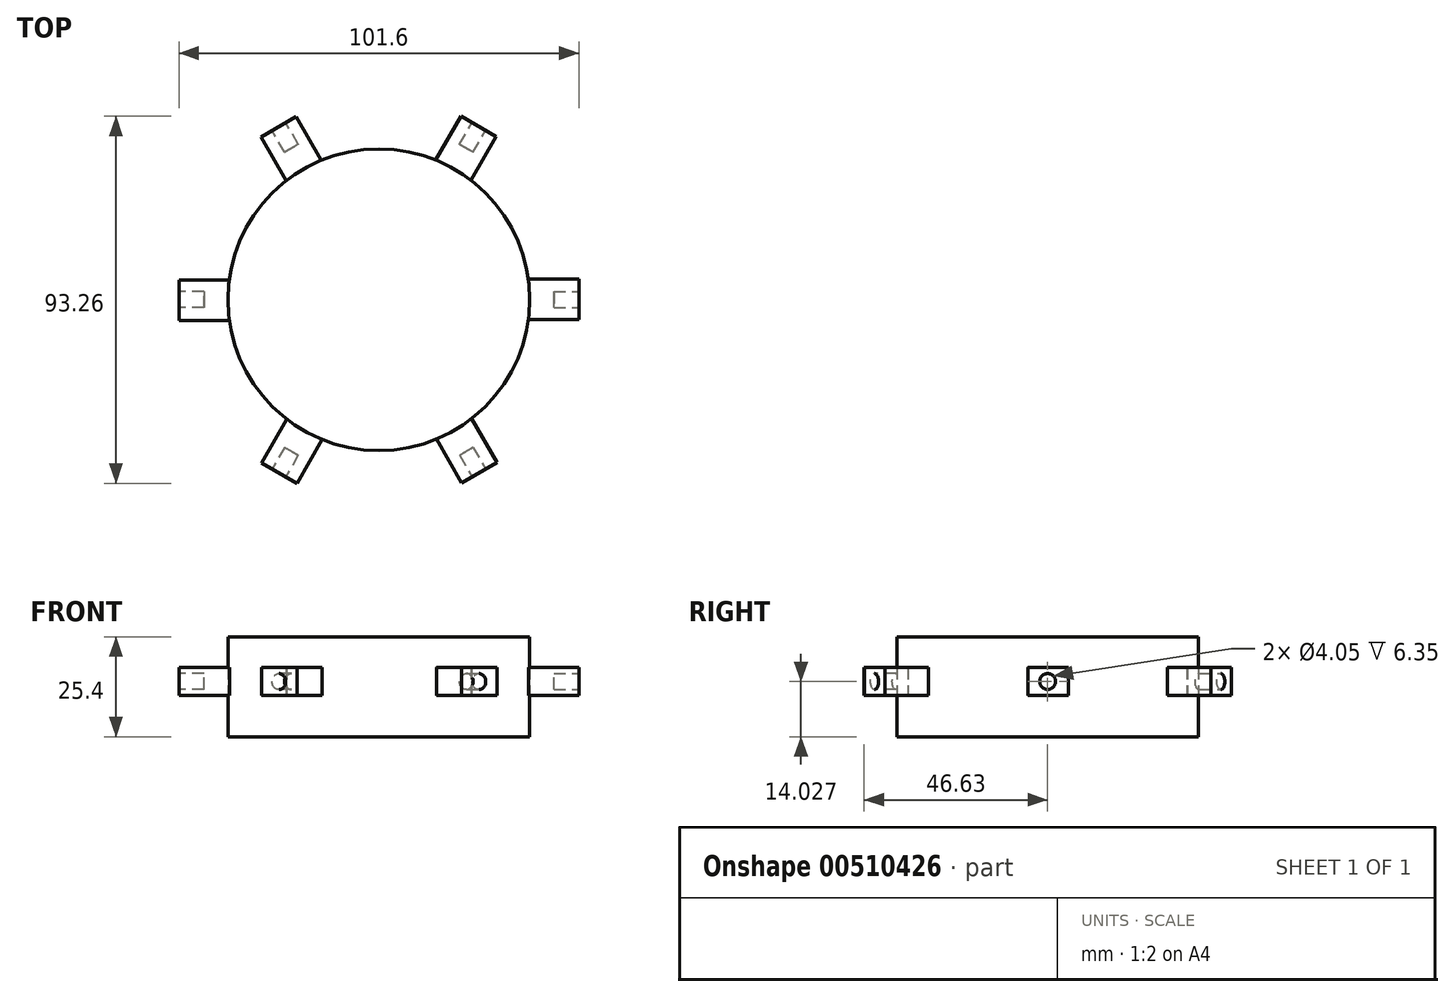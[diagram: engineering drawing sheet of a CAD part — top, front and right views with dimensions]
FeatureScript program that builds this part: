
annotation { "Feature Type Name" : "Feature", "Feature Type Description" : "" }
export const myFeature = defineFeature(function(context is Context, id is Id, definition is map)
    precondition{}
    {
        {
            var Q0;
            Q0=qCreatedBy(makeId("Top.planeOp"),FACE);
            var sketch = newSketch(context, id + "F0", { "sketchPlane" : qUnion([Q0])});
            skCircle(sketch, "E0", {"center": v(0, 0) * mm, "radius": 38.33 * mm});
            skSolve(sketch);
        }
        {
            var Q0;
            Q0=makeQuery(id+"F0.imprint","IMPRINT",FACE,{"disambiguationData":[TD([[makeQuery(id+"F0.imprint","IMPRINT",EDGE,{"derivedFrom":sQuery(id+"F0.wireOp",EDGE,"E0")}),1.0]])]});
            extrude(context, id + "F1", {"entities" : qUnion([Q0]), "depth" : 25.4 * mm});
        }
        {
            var Q0;
            Q0=qCreatedBy(makeId("Right.planeOp"),FACE);
            var sketch = newSketch(context, id + "F2", { "sketchPlane" : qUnion([Q0])});
            skLineSegment(sketch, "E1.bottom", {"start": v(-5.05, 17.62) * mm, "end": v(5.27, 17.62) * mm});
            skLineSegment(sketch, "E1.top", {"start": v(-5.05, 10.44) * mm, "end": v(5.27, 10.44) * mm});
            skLineSegment(sketch, "E1.left", {"start": v(-5.05, 17.62) * mm, "end": v(-5.05, 10.44) * mm});
            skLineSegment(sketch, "E1.right", {"start": v(5.27, 17.62) * mm, "end": v(5.27, 10.44) * mm});
            skSolve(sketch);
        }
        {
            var Q0;
            Q0 = qSketchRegion(id + "F2", true);
            extrude(context, id + "F3", {"entities" : qUnion([Q0]), "operationType" : NewBodyOperationType.ADD, "depth" : 50.8 * mm});
        }
        {
            var Q0;
            Q0=makeQuery(id+"F3.opExtrude","CAP_FACE",FACE,{"disambiguationData":[OSD([sQuery(id+"F2.wireOp",EDGE,"E1.bottom"),sQuery(id+"F2.wireOp",EDGE,"E1.top"),sQuery(id+"F2.wireOp",EDGE,"E1.left"),sQuery(id+"F2.wireOp",EDGE,"E1.right")])],"isStart":false});
            var sketch = newSketch(context, id + "F4", { "sketchPlane" : qUnion([Q0])});
            skCircle(sketch, "E2", {"center": v(0, 14.03) * mm, "radius": 2.02 * mm});
            skPoint(sketch, "E2.centerSnap0", {"position": v(5.27, 14.03) * mm});
            skSolve(sketch);
        }
        {
            var Q0;
            Q0 = qSketchRegion(id + "F4", true);
            extrude(context, id + "F5", {"entities" : qUnion([Q0]), "operationType" : NewBodyOperationType.REMOVE, "oppositeDirection" : true, "depth" : 6.35 * mm});
        }
        {
            var Q0;
            Q0=makeQuery(id+"F1.opExtrude","SWEPT_BODY",BODY,{"disambiguationData":[OSD([sQuery(id+"F0.wireOp",EDGE,"E0")])]});
            var Q1;
            Q1=makeQuery(id+"F1.opExtrude","CAP_EDGE",EDGE,{"disambiguationData":[OSD([sQuery(id+"F0.wireOp",EDGE,"E0")])],"isStart":false});
            circularPattern(context, id + "F6", {"entities" : qUnion([Q0]), "axis" : qUnion([Q1]), "angle" : 360 * degree, "instanceCount" : 6, "equalSpace" : true});
        }
    });
